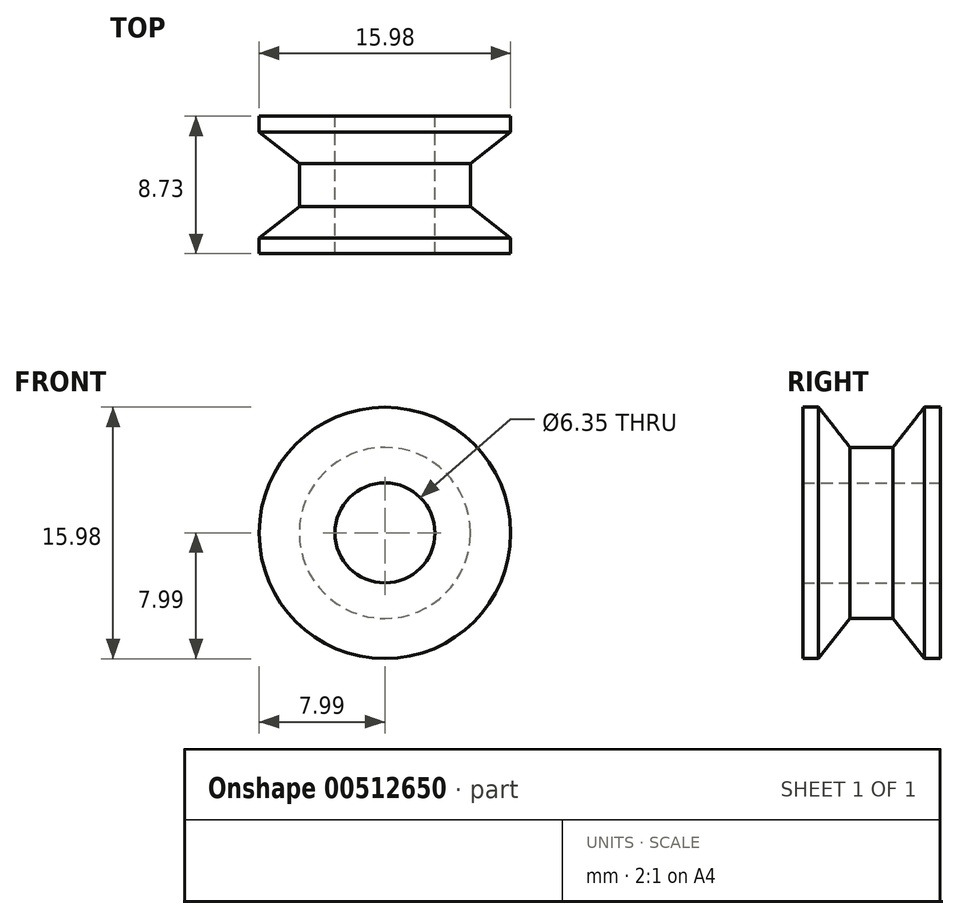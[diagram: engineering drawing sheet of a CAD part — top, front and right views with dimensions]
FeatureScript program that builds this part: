
annotation { "Feature Type Name" : "Feature", "Feature Type Description" : "" }
export const myFeature = defineFeature(function(context is Context, id is Id, definition is map)
    precondition{}
    {
        {
            var Q0;
            Q0=qCreatedBy(makeId("Right.planeOp"),FACE);
            var sketch = newSketch(context, id + "F0", { "sketchPlane" : qUnion([Q0])});
            skLineSegment(sketch, "E0", {"start": v(0, 0) * mm, "end": v(-8.73, 0) * mm, "construction": true});
            skLineSegment(sketch, "E1", {"start": v(-8.73, 7.99) * mm, "end": v(-7.73, 7.99) * mm});
            skLineSegment(sketch, "E2", {"start": v(0, 3.18) * mm, "end": v(0, 7.99) * mm});
            skLineSegment(sketch, "E3", {"start": v(0, 7.99) * mm, "end": v(-1, 7.99) * mm});
            skLineSegment(sketch, "E4", {"start": v(-1, 7.99) * mm, "end": v(-3, 5.43) * mm});
            skLineSegment(sketch, "E5", {"start": v(-3, 5.43) * mm, "end": v(-5.73, 5.43) * mm});
            skLineSegment(sketch, "E6", {"start": v(-5.73, 5.43) * mm, "end": v(-7.73, 7.99) * mm});
            skLineSegment(sketch, "E7", {"start": v(-7.73, 7.99) * mm, "end": v(-8.73, 7.99) * mm});
            skLineSegment(sketch, "E8", {"start": v(-8.73, 7.99) * mm, "end": v(-8.73, 3.17) * mm});
            skLineSegment(sketch, "E9", {"start": v(-8.73, 3.17) * mm, "end": v(0, 3.18) * mm});
            skLineSegment(sketch, "E10.trimOffspring", {"start": v(-1, 7.99) * mm, "end": v(0, 7.99) * mm});
            skPoint(sketch, "E11.orphan", {"position": v(-8.73, 0) * mm});
            skSolve(sketch);
        }
        {
            var Q0;
            Q0 = qSketchRegion(id + "F0", true);
            var Q1;
            Q1=sQuery(id+"F0.wireOp",EDGE,"E0");
            revolve(context, id + "F1", {"entities" : qUnion([Q0]), "axis" : qUnion([Q1]), "revolveType" : RevolveType.FULL});
        }
    });
